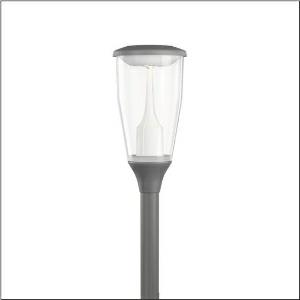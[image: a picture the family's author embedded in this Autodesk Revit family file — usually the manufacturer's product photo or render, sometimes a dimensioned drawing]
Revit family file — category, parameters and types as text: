
# Revit family: dl_11_iq___st1_2a_5xa5575ef14h000022_0b87
name_source: partatom
category: Lighting Fixtures
units: mm (PartAtom-declared; Revit-internal decimal feet)

## family parameters
Cut with Voids When Loaded = No
Host = Face
Light Source = No
Part Type = Normal
Room Calculation Point = No
Round Connector Dimension = Use Diameter
Shared = No

## types (1)
- --- (1 x LED, 1560 lm, 10.5 W, 3000K)
    Apparent Load = 11 VA
    CIE Flux Codes = 24 63 94 96 100
    Color Rendering = 70
    Color Temperature = 3000K
    Default Elevation = 1800 mm
    Description = DL 11 iQ, mast luminaire, Module 540 iQ-SR, primary light control with 3 zone facetted reflector, of plastic, silver coated, highly specular, structured, primary optical cover: cover, of PMMA, transparent, light distribution: ST1.2a, light emission: direct distribution, primary light characteristic: asymmetric, installation type: post-top, LED, High Power LED, rated luminous flux: 1.560lm, luminous efficacy: 149lm/W, light colour: 730, colour temperature: 3000K, control gear: iQ Street-Remote, control: Street-Remote, Auto-Match, Temp-Guard, Lumen-Switch, Night-Set, Smart-Wire, Light-Fading, Desk-Remote (wireless, voltage-free reading and setting of iQ features in the workshop via application-optimized NFC function/RFID function), optimised constant luminous flux control (CLO 2.0), mains connection: 220..240V, AC, 50/60Hz, connection cable pre-assembled, cable length: 5,5m, start of lifetime: 11W, end of service life: 11W, reduction: 5W, luminaire housing, upper part, of diecast aluminium, coated, Siteco® metallic grey (DB 702S), spigot size: 76mm (post-top), mounting height: 3..5m, post-top mast mounting element, of diecast aluminium, coated, Siteco® metallic grey (DB 702S), Module 540 iQ-SR, traffic white (RAL 9016), equipment: standard, protection rating (complete): IP66, insulation class (complete): insulation class II (safety insulation), certification: CE, ENEC, ENEC+, VDE, impact resistance: IK07, packaging unit: 1 piece

Light Distribution: ST1.2a
    Height = 665 mm
    Lamp = 1 x LED
    Lamp Light Flux = 1560 lm
    Lamp Power = 10.5 W
    Lamp count = 1
    Length = 334 mm
    Luminous efficacy = 149 lm/W
    Manufacturer = Siteco
    ModVariant = No
    Model = 5XA5575EF14H000022
    Number of Poles = 1
    OnlyDefault = Yes
    Power Factor = 1
    Product Name = DL 11 iQ | ST1.2a
    Product group = mast luminaire | pylon top
    ProductGroupID = 6100
    Protection Class = Protection class II
    Protection Degree = IP 66
    RLX_Detail_Level = 1
    RLX_Emergency_Light_Flux = 0 lm
    RLX_Emergency_Type = 0
    RLX_Emergency_Type_DB = No
    RlxData = <blob elided: 153033 chars, md5=239ea943>
    Socket = socket
    Standby Power = 0 W
    System Light Flux = 1560 lm
    System Power = 11 W
    Type Comments = factory setting: luminous flux: 100 % | dim-lin: 254 | 419 mA
    Type Image = l_1258354.jpg
    URL = http://relux.com
    VarID = @adj_094896
    Voltage = 0 V
    Weight = 0.00 kg
    Width = 0 mm  [stored 0 ft]

note: [stored X ft] marks values corroborated as IEEE doubles in the binary element streams (Revit-internal decimal feet)

## geometry (parser evidence)
native form markers: Blend x4, Sweep x9
no freeform markers — native parametric forms only
